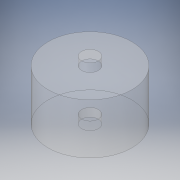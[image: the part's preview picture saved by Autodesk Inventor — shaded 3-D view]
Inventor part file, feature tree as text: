
AUTODESK INVENTOR PART (.ipt)
format: ipt  version: 2018 (Build 220112000, 112)  size: 110,080 bytes
history: native  units: in
note: dims shown in document units (in); Inventor stores cm internally (conversion verified against a paired STEP export)
features: extrude x2, sketch x2, hole x1
ambient origin geometry x8: Origin, YZ Plane, XZ Plane, XY Plane, X Axis, Y Axis, Z Axis, Center Point
bodies: Solid1 (feature_tree)
feature tree (5):
  extrude  "Extrusion1"  Depth=1.189in TaperAngle=0.0deg
  hole  "Hole1"  [1 undecoded]
  extrude  "Extrusion2"  [1 undecoded]
  sketch  "Sketch1"  dims[d0=1.9685in d1=1.189in d2=0.0in]
  sketch  "Sketch2"  dims[d3=0.3937in d4=0.3937in d5=0.3937in d6=0.2362in d7=0.1575in d8=0.0787in d9=90.0deg d10=0.1969in d11=0.0in d12=0.1969in d13=0.0in]
note: 2 required parameter values undecoded (feature->parameter linkage not recoverable at this tier; creation-order binding heuristic only, values carry confidence <= 0.55)
